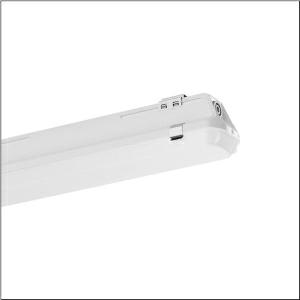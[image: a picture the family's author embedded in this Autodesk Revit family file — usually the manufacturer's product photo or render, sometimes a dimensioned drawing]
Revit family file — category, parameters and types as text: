
# Revit family: monsun_11_51fp20dp460l
name_source: partatom
category: Lighting Fixtures
units: mm (PartAtom-declared; Revit-internal decimal feet)

## family parameters
Cut with Voids When Loaded = No
Host = Face
Light Source = No
Part Type = Normal
Room Calculation Point = No
Round Connector Dimension = Use Diameter
Shared = No

## types (1)
- --- (1 x LED, 5450 lm, 31.5 W, 4000K)
    Apparent Load = 32 VA
    CIE Flux Codes = 45 75 93 94 100
    Color Rendering = 80
    Color Temperature = 4000K
    Default Elevation = 1800 mm
    Description = Monsun 11, damp-proof luminaire, chain hanger, primary optical cover: enclosure, of PC, light emission: direct distribution, primary light characteristic: symmetric, installation type: suspended mounting, surface-mounted, horizontal mounting, vertical mounting, LED, rated luminous flux: 5.450lm, luminous efficacy: 173lm/W, light colour: 840, colour temperature: 4000K, control gear: DALI 2, with terminal, 5-pole, max. 2.5mm², mains connection: 220..240V, AC, 50/60Hz, rated input power: 32W, luminaire housing, of glass-fibre reinforced polyester, uncoated, bright grey, incl. chain hanger, length: 1.590mm, width: 90mm, height: 88mm, clip for enclosure, of stainless steel (V2A), ceiling mounting element, of stainless steel (V2A), chain hanger, of stainless steel (V2A), protection rating (complete): IP66, insulation class (complete): insulation class I (protective earthing), certification: CE, ENEC, VDE, UKCA, protection symbol: D, impact resistance: IK08, permissible operating ambient temperature: -25..+35°C, standard: EN 50419, EN 60598-2-1, corresponds to IFS (International Featured Standards) requirements for safety and quality in the food industry, for indoor or canopied outdoor use, no direct snow, no direct sun, no direct rain, LABS conformity tested according to VDMA 24364:2018-05, contact your sales advisor before using the luminaires in applications with unclear chemical exposure, large temperature fluctuations or condensation-forming humidity, packaging unit: 1 piece
    Height = 89 mm
    Lamp = 1 x LED
    Lamp Light Flux = 5450 lm
    Lamp Power = 31.5 W
    Lamp count = 1
    Length = 1590 mm
    Luminous efficacy = 173 lm/W
    Manufacturer = Siteco
    ModVariant = No
    Model = 51FP20DP460L
    Mounting Place = Ceiling
    Mounting Type = Surface mounted
    Number of Poles = 1
    OnlyDefault = Yes
    Power Factor = 1
    Product Name = Monsun 11
    Product group = damp-proof luminaire
    ProductGroupID = 300
    Protection Class = Protection class I
    Protection Degree = IP 66
    RLX_Detail_Level = 1
    RLX_Emergency_Light_Flux = 0 lm
    RLX_Emergency_Type = 0
    RLX_Emergency_Type_DB = No
    RlxData = <blob elided: 92281 chars, md5=a630fde4>
    Socket = socket
    Standby Power = 0 W
    System Light Flux = 5450 lm
    System Power = 32 W
    Type Comments = factory setting: luminous flux: 100 % | dim-lin: 254 | 219 mA
    Type Image = l_1349237.jpg
    URL = http://relux.com
    VarID = @adj_035809
    Voltage = 0 V
    Weight = 0.00 kg
    Width = 90 mm

## geometry (parser evidence)
native form markers: Blend x4, Sweep x12
no freeform markers — native parametric forms only
